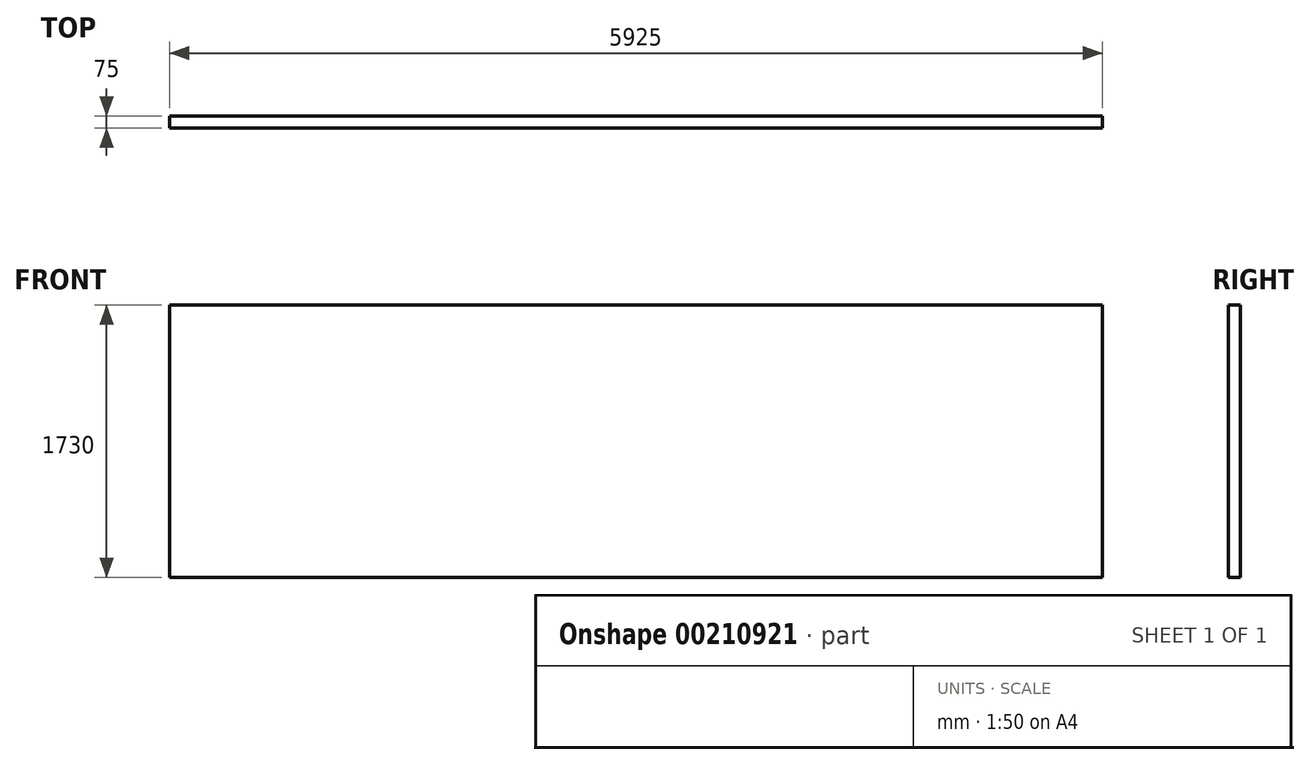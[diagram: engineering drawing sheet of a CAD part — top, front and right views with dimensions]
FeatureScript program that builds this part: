
annotation { "Feature Type Name" : "Feature", "Feature Type Description" : "" }
export const myFeature = defineFeature(function(context is Context, id is Id, definition is map)
    precondition{}
    {
        {
            var Q0;
            Q0=qCreatedBy(makeId("Front.planeOp"),FACE);
            var sketch = newSketch(context, id + "F0", { "sketchPlane" : qUnion([Q0])});
            skLineSegment(sketch, "E0.bottom", {"start": v(0, 0) * mm, "end": v(5925, 0) * mm});
            skLineSegment(sketch, "E0.right", {"start": v(5925, 0) * mm, "end": v(5925, 1730) * mm});
            skLineSegment(sketch, "E1", {"start": v(0, 1730) * mm, "end": v(5925, 1730) * mm});
            skLineSegment(sketch, "E2", {"start": v(0, 0) * mm, "end": v(0, 1730) * mm});
            skSolve(sketch);
        }
        {
            var Q0;
            Q0=makeQuery(id+"F0.imprint","IMPRINT",FACE,{"disambiguationData":[TD([[makeQuery(id+"F0.imprint","IMPRINT",EDGE,{"derivedFrom":sQuery(id+"F0.wireOp",EDGE,"E0.bottom")}),1.0]])]});
            extrude(context, id + "F1", {"entities" : qUnion([Q0]), "depth" : 75 * mm});
        }
    });
